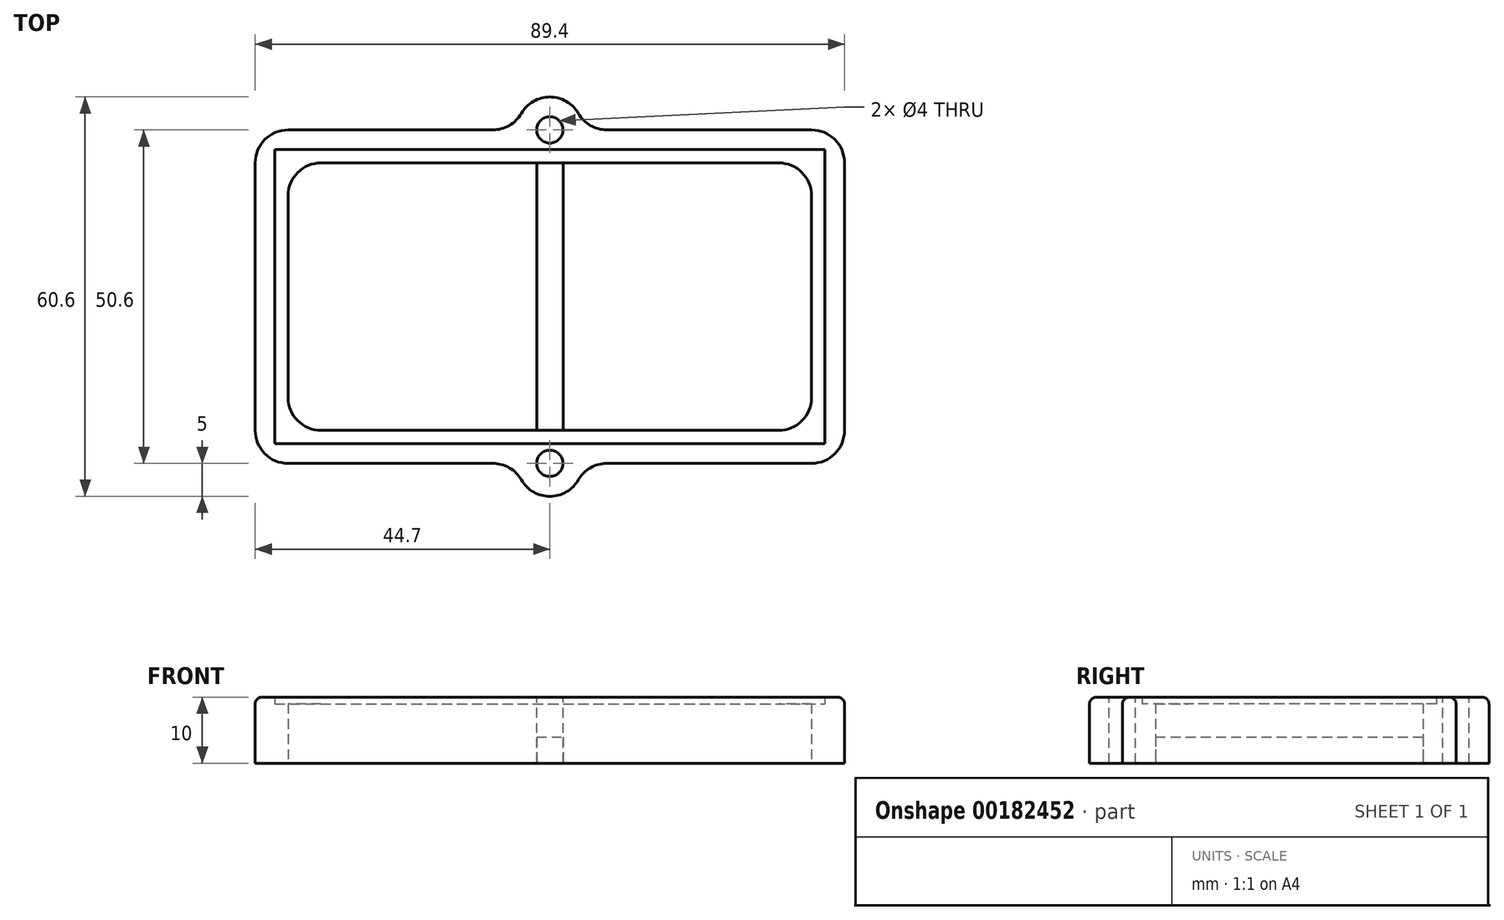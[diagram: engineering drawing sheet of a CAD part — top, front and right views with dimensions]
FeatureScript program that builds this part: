
annotation { "Feature Type Name" : "Feature", "Feature Type Description" : "" }
export const myFeature = defineFeature(function(context is Context, id is Id, definition is map)
    precondition{}
    {
        {
            var Q0;
            Q0=qCreatedBy(makeId("Top.planeOp"),FACE);
            var sketch = newSketch(context, id + "F0", { "sketchPlane" : qUnion([Q0])});
            skLineSegment(sketch, "E0.bottom", {"start": v(-41.7, 22.3) * mm, "end": v(41.7, 22.3) * mm});
            skLineSegment(sketch, "E0.top", {"start": v(-41.7, -22.3) * mm, "end": v(41.7, -22.3) * mm});
            skLineSegment(sketch, "E0.left", {"start": v(-41.7, 22.3) * mm, "end": v(-41.7, -22.3) * mm});
            skLineSegment(sketch, "E0.right", {"start": v(41.7, 22.3) * mm, "end": v(41.7, -22.3) * mm});
            skPoint(sketch, "E0.middle", {"position": v(0, 0) * mm});
            skLineSegment(sketch, "E1.bottom", {"start": v(-39.7, 20.3) * mm, "end": v(39.7, 20.3) * mm});
            skLineSegment(sketch, "E1.top", {"start": v(-39.7, -20.3) * mm, "end": v(39.7, -20.3) * mm});
            skLineSegment(sketch, "E1.left", {"start": v(-39.7, 20.3) * mm, "end": v(-39.7, -20.3) * mm});
            skLineSegment(sketch, "E1.right", {"start": v(39.7, 20.3) * mm, "end": v(39.7, -20.3) * mm});
            skLineSegment(sketch, "E2.bottom", {"start": v(-44.7, 25.3) * mm, "end": v(44.7, 25.3) * mm});
            skLineSegment(sketch, "E2.top", {"start": v(-44.7, -25.3) * mm, "end": v(44.7, -25.3) * mm});
            skLineSegment(sketch, "E2.left", {"start": v(-44.7, 25.3) * mm, "end": v(-44.7, -25.3) * mm});
            skLineSegment(sketch, "E2.right", {"start": v(44.7, 25.3) * mm, "end": v(44.7, -25.3) * mm});
            skLineSegment(sketch, "E3", {"start": v(-2, -20.3) * mm, "end": v(-2, 20.3) * mm});
            skLineSegment(sketch, "E4", {"start": v(2, -20.3) * mm, "end": v(2, 20.3) * mm});
            skLineSegment(sketch, "E5", {"start": v(0, -30.3) * mm, "end": v(0, 30.3) * mm, "construction": true});
            skPoint(sketch, "E6", {"position": v(0, 25.3) * mm});
            skPoint(sketch, "E7", {"position": v(0, -22.3) * mm});
            skArc(sketch, "E8", {"start": v(-5, -25.3) * mm, "mid": v(0, -30.3) * mm, "end": v(5, -25.3) * mm});
            skArc(sketch, "E9", {"start": v(5, 25.3) * mm, "mid": v(0, 30.3) * mm, "end": v(-5, 25.3) * mm});
            skSolve(sketch);
        }
        {
            var Q0;
            Q0=makeQuery(id+"F0.imprint","IMPRINT",FACE,{"disambiguationData":[TD([[makeQuery(id+"F0.imprint","IMPRINT",EDGE,{"derivedFrom":sQuery(id+"F0.wireOp",EDGE,"E0.bottom")}),-1.0]])]});
            extrude(context, id + "F1", {"entities" : qUnion([Q0]), "depth" : 9 * mm, "offsetDistance" : 25 * mm});
        }
        {
            var Q0;
            Q0=makeQuery(id+"F0.imprint","IMPRINT",FACE,{"disambiguationData":[TD([[makeQuery(id+"F0.imprint","IMPRINT",EDGE,{"derivedFrom":sQuery(id+"F0.wireOp",EDGE,"E0.bottom")}),1.0]])]});
            var Q1;
            {var subQ0=sQuery(id+"F0.wireOp",EDGE,"E8");Q1=makeQuery(id+"F0.imprint","IMPRINT",FACE,{"disambiguationData":[TD([[makeQuery(id+"F0.imprint","IMPRINT",EDGE,{"derivedFrom":subQ0}),1.0]])]});}
            var Q2;
            {var subQ0=sQuery(id+"F0.wireOp",EDGE,"E9");Q2=makeQuery(id+"F0.imprint","IMPRINT",FACE,{"disambiguationData":[TD([[makeQuery(id+"F0.imprint","IMPRINT",EDGE,{"derivedFrom":subQ0}),1.0]])]});}
            extrude(context, id + "F2", {"entities" : qUnion([Q0, Q1, Q2]), "operationType" : NewBodyOperationType.ADD, "depth" : 10 * mm, "offsetDistance" : 25 * mm});
        }
        {
            var Q0;
            {var subQ2=sQuery(id+"F0.wireOp",EDGE,"E3");Q0=makeQuery(id+"F0.imprint","IMPRINT",FACE,{"disambiguationData":[TD([[makeQuery(id+"F0.imprint","IMPRINT",EDGE,{"derivedFrom":subQ2}),-1.0]])]});}
            extrude(context, id + "F3", {"entities" : qUnion([Q0]), "operationType" : NewBodyOperationType.ADD, "depth" : 4 * mm, "offsetDistance" : 25 * mm});
        }
        {
            var Q0;
            Q0=sQuery(id+"F0.wireOp",VERTEX,"E6");
            var Q1;
            Q1=sQuery(id+"F0.wireOp",VERTEX,"E8.center");
            var Q2;
            Q2=makeQuery(id+"F1.opExtrude","SWEPT_BODY",BODY,{"disambiguationData":[OSD([sQuery(id+"F0.wireOp",EDGE,"E0.bottom"),sQuery(id+"F0.wireOp",EDGE,"E0.top"),sQuery(id+"F0.wireOp",EDGE,"E0.left"),sQuery(id+"F0.wireOp",EDGE,"E0.right"),sQuery(id+"F0.wireOp",EDGE,"E1.bottom"),sQuery(id+"F0.wireOp",EDGE,"E1.top"),sQuery(id+"F0.wireOp",EDGE,"E1.left"),sQuery(id+"F0.wireOp",EDGE,"E1.right")])]});
            hole(context, id + "F4", {"style" : HoleStyle.SIMPLE, "endStyle" : HoleEndStyle.BLIND, "oppositeDirection" : true, "holeDiameter" : 4 * mm, "majorDiameter" : 5 * mm, "holeDepth" : 15 * mm, "tappedDepth" : 12 * mm, "tapClearance" : 3, "locations" : qUnion([Q0, Q1]), "scope" : qUnion([Q2])});
        }
        {
            var Q0;
            Q0=makeQuery(id+"F2.opExtrude","SWEPT_EDGE",EDGE,{"disambiguationData":[OSD([sQuery(id+"F0.wireOp",EDGE,"E2.bottom"),sQuery(id+"F0.wireOp",EDGE,"E2.left")])]});
            var Q1;
            {var subQ0=sQuery(id+"F0.wireOp",EDGE,"E9");var subQ1=sQuery(id+"F0.wireOp",EDGE,"E2.bottom");Q1=makeQuery(id+"F2.opExtrude","SWEPT_EDGE",EDGE,{"disambiguationData":[OSD([subQ1,subQ0]),TDD([makeQuery(id+"F0.imprint","INTERSECT",VERTEX,{"disambiguationData":[OD(0.0)],"derivedFrom":[subQ1,subQ0]})])]});}
            var Q2;
            {var subQ0=sQuery(id+"F0.wireOp",EDGE,"E9");var subQ1=sQuery(id+"F0.wireOp",EDGE,"E2.bottom");Q2=makeQuery(id+"F2.opExtrude","SWEPT_EDGE",EDGE,{"disambiguationData":[OSD([subQ1,subQ0]),TDD([makeQuery(id+"F0.imprint","INTERSECT",VERTEX,{"disambiguationData":[OD(1.0)],"derivedFrom":[subQ1,subQ0]})])]});}
            var Q3;
            Q3=makeQuery(id+"F2.opExtrude","SWEPT_EDGE",EDGE,{"disambiguationData":[OSD([sQuery(id+"F0.wireOp",EDGE,"E2.bottom"),sQuery(id+"F0.wireOp",EDGE,"E2.right")])]});
            var Q4;
            Q4=makeQuery(id+"F2.opExtrude","SWEPT_EDGE",EDGE,{"disambiguationData":[OSD([sQuery(id+"F0.wireOp",EDGE,"E2.top"),sQuery(id+"F0.wireOp",EDGE,"E2.right")])]});
            var Q5;
            {var subQ0=sQuery(id+"F0.wireOp",EDGE,"E8");var subQ1=sQuery(id+"F0.wireOp",EDGE,"E2.top");Q5=makeQuery(id+"F2.opExtrude","SWEPT_EDGE",EDGE,{"disambiguationData":[OSD([subQ1,subQ0]),TDD([makeQuery(id+"F0.imprint","INTERSECT",VERTEX,{"disambiguationData":[OD(0.0)],"derivedFrom":[subQ1,subQ0]})])]});}
            var Q6;
            {var subQ0=sQuery(id+"F0.wireOp",EDGE,"E8");var subQ1=sQuery(id+"F0.wireOp",EDGE,"E2.top");Q6=makeQuery(id+"F2.opExtrude","SWEPT_EDGE",EDGE,{"disambiguationData":[OSD([subQ1,subQ0]),TDD([makeQuery(id+"F0.imprint","INTERSECT",VERTEX,{"disambiguationData":[OD(1.0)],"derivedFrom":[subQ1,subQ0]})])]});}
            var Q7;
            Q7=makeQuery(id+"F2.opExtrude","SWEPT_EDGE",EDGE,{"disambiguationData":[OSD([sQuery(id+"F0.wireOp",EDGE,"E2.top"),sQuery(id+"F0.wireOp",EDGE,"E2.left")])]});
            var Q8;
            Q8=makeQuery(id+"F3.opExtrude","SWEPT_EDGE",EDGE,{"disambiguationData":[OSD([sQuery(id+"F0.wireOp",EDGE,"E1.bottom"),sQuery(id+"F0.wireOp",EDGE,"E4")])]});
            var Q9;
            Q9=makeQuery(id+"F3.opExtrude","SWEPT_EDGE",EDGE,{"disambiguationData":[OSD([sQuery(id+"F0.wireOp",EDGE,"E1.bottom"),sQuery(id+"F0.wireOp",EDGE,"E3")])]});
            var Q10;
            Q10=makeQuery(id+"F3.opExtrude","SWEPT_EDGE",EDGE,{"disambiguationData":[OSD([sQuery(id+"F0.wireOp",EDGE,"E1.top"),sQuery(id+"F0.wireOp",EDGE,"E4")])]});
            var Q11;
            Q11=makeQuery(id+"F3.opExtrude","SWEPT_EDGE",EDGE,{"disambiguationData":[OSD([sQuery(id+"F0.wireOp",EDGE,"E1.top"),sQuery(id+"F0.wireOp",EDGE,"E3")])]});
            var Q12;
            Q12=makeQuery(id+"F1.opExtrude","SWEPT_EDGE",EDGE,{"disambiguationData":[OSD([sQuery(id+"F0.wireOp",EDGE,"E1.bottom"),sQuery(id+"F0.wireOp",EDGE,"E1.right")])]});
            var Q13;
            Q13=makeQuery(id+"F1.opExtrude","SWEPT_EDGE",EDGE,{"disambiguationData":[OSD([sQuery(id+"F0.wireOp",EDGE,"E1.bottom"),sQuery(id+"F0.wireOp",EDGE,"E1.left")])]});
            var Q14;
            Q14=makeQuery(id+"F1.opExtrude","SWEPT_EDGE",EDGE,{"disambiguationData":[OSD([sQuery(id+"F0.wireOp",EDGE,"E1.top"),sQuery(id+"F0.wireOp",EDGE,"E1.left")])]});
            var Q15;
            Q15=makeQuery(id+"F1.opExtrude","SWEPT_EDGE",EDGE,{"disambiguationData":[OSD([sQuery(id+"F0.wireOp",EDGE,"E1.top"),sQuery(id+"F0.wireOp",EDGE,"E1.right")])]});
            fillet(context, id + "F5", {"entities" : qUnion([Q0, Q1, Q2, Q3, Q4, Q5, Q6, Q7, Q8, Q9, Q10, Q11, Q12, Q13, Q14, Q15]), "tangentPropagation" : true, "radius" : 5 * mm, "defaultsChanged" : false, "vertexSettings" : [], "allowEdgeOverflow" : false});
        }
        {
            var Q0;
            {var subQ0=sQuery(id+"F0.wireOp",EDGE,"E2.left");var subQ1=sQuery(id+"F0.wireOp",EDGE,"E2.bottom");Q0=makeQuery(id+"F5.opFillet","BLEND_EDGE",EDGE,{"blendedFrom":[makeQuery(id+"F2.opExtrude","SWEPT_EDGE",EDGE,{"disambiguationData":[OSD([subQ1,subQ0])]}),makeQuery(id+"F2.opExtrude","CAP_FACE",FACE,{"disambiguationData":[OSD([sQuery(id+"F0.wireOp",EDGE,"E0.bottom"),sQuery(id+"F0.wireOp",EDGE,"E0.top"),sQuery(id+"F0.wireOp",EDGE,"E0.left"),sQuery(id+"F0.wireOp",EDGE,"E0.right"),subQ1,sQuery(id+"F0.wireOp",EDGE,"E2.top"),subQ0,sQuery(id+"F0.wireOp",EDGE,"E2.right"),sQuery(id+"F0.wireOp",EDGE,"E8"),sQuery(id+"F0.wireOp",EDGE,"E9")])],"isStart":false})],"blendedInto":[makeQuery(id+"F2.opExtrude","CAP_FACE",FACE,{"disambiguationData":[OSD([sQuery(id+"F0.wireOp",EDGE,"E0.bottom"),sQuery(id+"F0.wireOp",EDGE,"E0.top"),sQuery(id+"F0.wireOp",EDGE,"E0.left"),sQuery(id+"F0.wireOp",EDGE,"E0.right"),subQ1,sQuery(id+"F0.wireOp",EDGE,"E2.top"),subQ0,sQuery(id+"F0.wireOp",EDGE,"E2.right"),sQuery(id+"F0.wireOp",EDGE,"E8"),sQuery(id+"F0.wireOp",EDGE,"E9")])],"isStart":false})]});}
            fillet(context, id + "F6", {"entities" : qUnion([Q0]), "tangentPropagation" : true, "radius" : 1 * mm, "defaultsChanged" : true, "vertexSettings" : [], "allowEdgeOverflow" : false});
        }
    });
